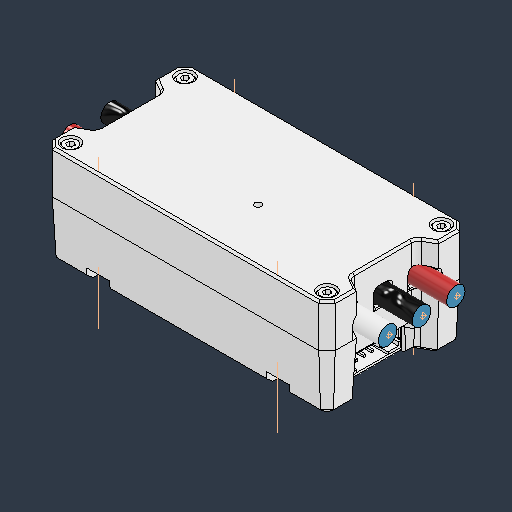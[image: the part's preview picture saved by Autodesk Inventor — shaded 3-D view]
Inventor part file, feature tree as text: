
AUTODESK INVENTOR PART (.ipt)
format: ipt  version: 2024.3 (Build 283343000, 343)  size: 2,232,832 bytes
history: native  units: in
note: dims shown in document units (in); Inventor stores cm internally (conversion verified against a paired STEP export)
features: other x22, sketch x4
ambient origin geometry x8: Origin, YZ Plane, XZ Plane, XY Plane, X Axis, Y Axis, Z Axis, Center Point
bodies: Solid1 (feature_tree), Solid2 (feature_tree), Solid3 (feature_tree), Solid4 (feature_tree), Solid5 (feature_tree), Solid6 (feature_tree), Solid7 (feature_tree), Solid8 (feature_tree), Solid9 (feature_tree), Solid10 (feature_tree), Solid11 (feature_tree), Solid12 (feature_tree), Solid13 (feature_tree), Solid14 (feature_tree), Solid15 (feature_tree), Solid16 (feature_tree), Solid17 (feature_tree), Solid18 (feature_tree)
feature tree (26):
  other  "Work Axis1"
  other  "Work Axis2"
  other  "Work Axis3"
  other  "Work Axis4"
  sketch  "Sketch1"
  sketch  "Sketch2"
  sketch  "Sketch3"
  sketch  "Sketch4"
  parser-record x1  (decoder bookkeeping rows leaked as tree rows — omitted from the tree; the rows remain in map.json)
  other  "NONE:1"
  other  "NONE:2"
  other  "NONE:3"
  other  "NONE:4"
  other  "NONE:5"
  other  "NONE:6"
  other  "NONE:7"
  other  "NONE:8"
  other  "NONE:9"
  other  "NONE:10"
  other  "NONE:11"
  other  "NONE:12"
  other  "Cut-Extrude1[1]"
  other  "Cut-Extrude1[2]"
  other  "Cut-Extrude1[3]"
  other  "Cut-Extrude1[4]"
  other  "Cut-Extrude1[5]"
